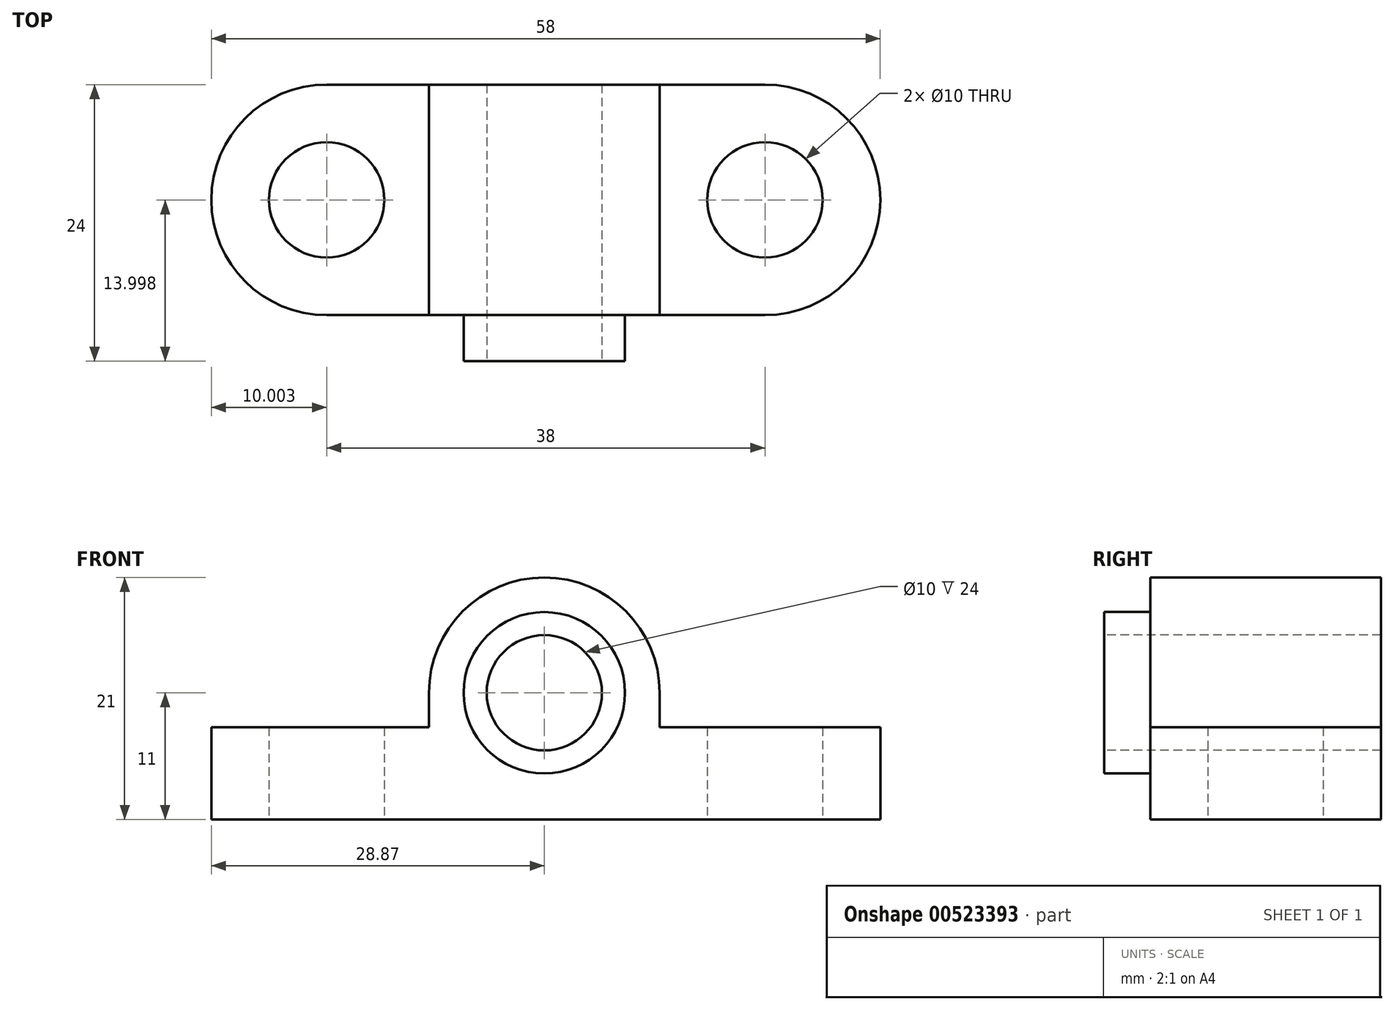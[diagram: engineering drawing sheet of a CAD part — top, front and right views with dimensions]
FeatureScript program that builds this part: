
annotation { "Feature Type Name" : "Feature", "Feature Type Description" : "" }
export const myFeature = defineFeature(function(context is Context, id is Id, definition is map)
    precondition{}
    {
        {
            var Q0;
            Q0=qCreatedBy(makeId("Top.planeOp"),FACE);
            var sketch = newSketch(context, id + "F0", { "sketchPlane" : qUnion([Q0])});
            skLineSegment(sketch, "E0", {"start": v(-18.87, -11.01) * mm, "end": v(19.13, -11.01) * mm});
            skLineSegment(sketch, "E1", {"start": v(-18.87, 8.99) * mm, "end": v(19.13, 8.99) * mm});
            skArc(sketch, "E2", {"start": v(-18.87, 8.99) * mm, "mid": v(-28.87, -1.01) * mm, "end": v(-18.87, -11.01) * mm});
            skArc(sketch, "E3", {"start": v(19.13, -11.01) * mm, "mid": v(29.13, -1.01) * mm, "end": v(19.13, 8.99) * mm});
            skCircle(sketch, "E4", {"center": v(-18.87, -1.01) * mm, "radius": 5 * mm});
            skCircle(sketch, "E5", {"center": v(19.13, -1.01) * mm, "radius": 5 * mm});
            skSolve(sketch);
        }
        {
            var Q0;
            Q0 = qSketchRegion(id + "F0", true);
            extrude(context, id + "F1", {"entities" : qUnion([Q0]), "depth" : 8 * mm, "offsetDistance" : 25.4 * mm});
        }
        {
            var Q0;
            Q0=makeQuery(id+"F1.opExtrude","SWEPT_FACE",FACE,{"disambiguationData":[OSD([sQuery(id+"F0.wireOp",EDGE,"E0")])]});
            var sketch = newSketch(context, id + "F2", { "sketchPlane" : qUnion([Q0])});
            skLineSegment(sketch, "E6", {"start": v(-10, 8) * mm, "end": v(0, 8) * mm});
            skLineSegment(sketch, "E7", {"start": v(0, 8) * mm, "end": v(10, 8) * mm});
            skLineSegment(sketch, "E8", {"start": v(10, 8) * mm, "end": v(10, 11) * mm});
            skLineSegment(sketch, "E9", {"start": v(10, 11) * mm, "end": v(0, 11) * mm});
            skLineSegment(sketch, "E10", {"start": v(0, 11) * mm, "end": v(-10, 11) * mm});
            skLineSegment(sketch, "E11", {"start": v(-10, 11) * mm, "end": v(-10, 8) * mm});
            skArc(sketch, "E12", {"start": v(10, 11) * mm, "mid": v(0, 21) * mm, "end": v(-10, 11) * mm});
            skSolve(sketch);
        }
        {
            var Q0;
            Q0 = qSketchRegion(id + "F2", true);
            extrude(context, id + "F3", {"entities" : qUnion([Q0]), "operationType" : NewBodyOperationType.ADD, "oppositeDirection" : true, "depth" : 20 * mm, "offsetDistance" : 25.4 * mm});
        }
        {
            var Q0;
            Q0=makeQuery(id+"F3.boolean.opBoolean","MERGE",FACE,{"derivedFrom":[makeQuery(id+"F1.opExtrude","SWEPT_FACE",FACE,{"disambiguationData":[OSD([sQuery(id+"F0.wireOp",EDGE,"E0")])]}),makeQuery(id+"F3.opExtrude","CAP_FACE",FACE,{"disambiguationData":[OSD([sQuery(id+"F2.wireOp",EDGE,"E6"),sQuery(id+"F2.wireOp",EDGE,"E7"),sQuery(id+"F2.wireOp",EDGE,"E8"),sQuery(id+"F2.wireOp",EDGE,"E11"),sQuery(id+"F2.wireOp",EDGE,"E12")])],"isStart":true})]});
            var sketch = newSketch(context, id + "F4", { "sketchPlane" : qUnion([Q0])});
            skCircle(sketch, "E13", {"center": v(0, 11) * mm, "radius": 7 * mm});
            skCircle(sketch, "E14", {"center": v(0, 11) * mm, "radius": 5 * mm});
            skSolve(sketch);
        }
        {
            var Q0;
            Q0=makeQuery(id+"F4.imprint","IMPRINT",FACE,{"disambiguationData":[TD([[makeQuery(id+"F4.imprint","IMPRINT",EDGE,{"derivedFrom":sQuery(id+"F4.wireOp",EDGE,"E14")}),1.0]])]});
            extrude(context, id + "F5", {"entities" : qUnion([Q0]), "operationType" : NewBodyOperationType.REMOVE, "endBound" : BoundingType.THROUGH_ALL, "oppositeDirection" : true, "depth" : 25.4 * mm, "offsetDistance" : 25.4 * mm});
        }
        {
            var Q0;
            Q0 = qSketchRegion(id + "F4", true);
            extrude(context, id + "F6", {"entities" : qUnion([Q0]), "operationType" : NewBodyOperationType.ADD, "depth" : 4 * mm, "offsetDistance" : 25.4 * mm});
        }
    });
